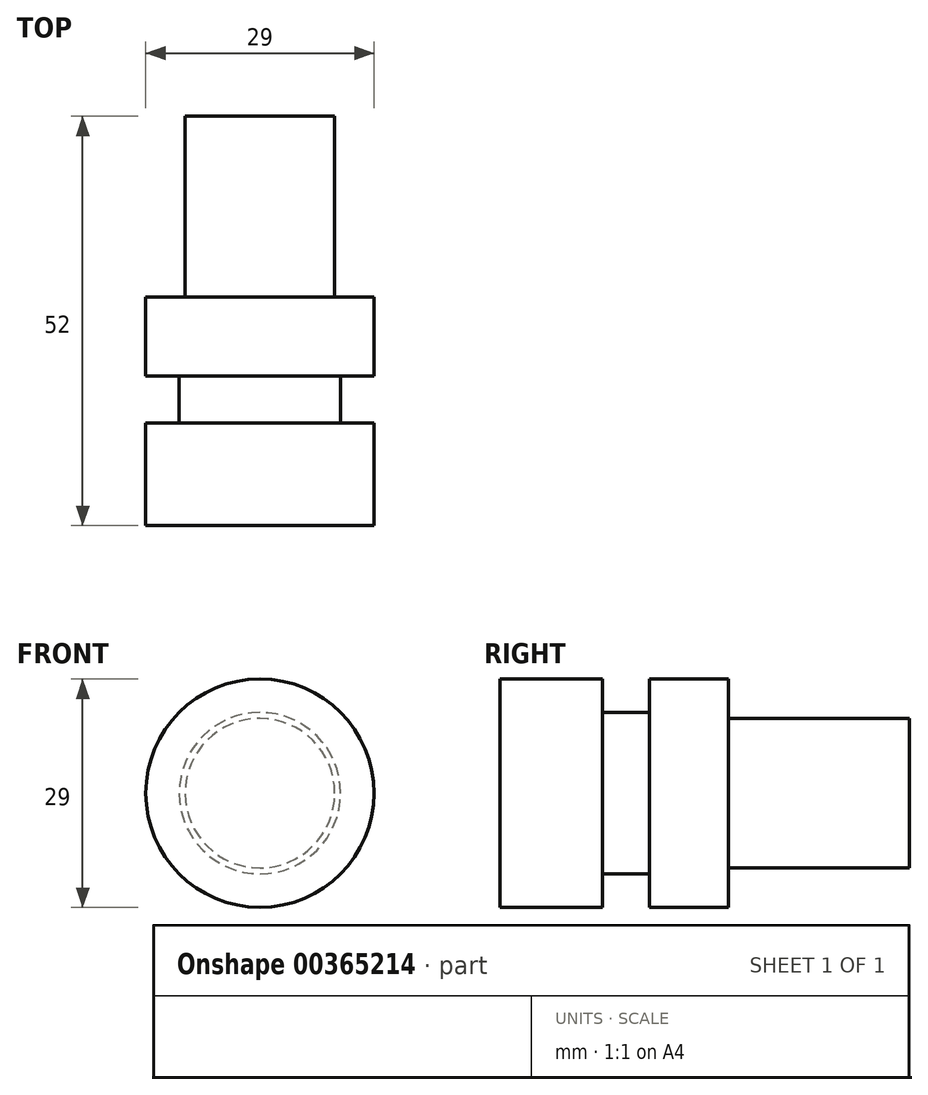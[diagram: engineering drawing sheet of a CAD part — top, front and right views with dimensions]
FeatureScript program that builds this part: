
annotation { "Feature Type Name" : "Feature", "Feature Type Description" : "" }
export const myFeature = defineFeature(function(context is Context, id is Id, definition is map)
    precondition{}
    {
        {
            var Q0;
            Q0=qCreatedBy(makeId("Front.planeOp"),FACE);
            var sketch = newSketch(context, id + "F0", { "sketchPlane" : qUnion([Q0])});
            skCircle(sketch, "E0", {"center": v(0, 0) * mm, "radius": 10.25 * mm});
            skSolve(sketch);
        }
        {
            var Q0;
            Q0 = qSketchRegion(id + "F0", true);
            extrude(context, id + "F1", {"entities" : qUnion([Q0]), "depth" : 6 * mm});
        }
        {
            var Q0;
            Q0=makeQuery(id+"F1.opExtrude","CAP_FACE",FACE,{"disambiguationData":[OSD([sQuery(id+"F0.wireOp",EDGE,"E0")])],"isStart":false});
            var sketch = newSketch(context, id + "F2", { "sketchPlane" : qUnion([Q0])});
            skCircle(sketch, "E1", {"center": v(0, 0) * mm, "radius": 14.5 * mm});
            skSolve(sketch);
        }
        {
            var Q0;
            Q0 = qSketchRegion(id + "F2", true);
            extrude(context, id + "F3", {"entities" : qUnion([Q0]), "operationType" : NewBodyOperationType.ADD, "depth" : 13 * mm});
        }
        {
            var Q0;
            Q0=makeQuery(id+"F1.opExtrude","CAP_FACE",FACE,{"disambiguationData":[OSD([sQuery(id+"F0.wireOp",EDGE,"E0")])],"isStart":true});
            var sketch = newSketch(context, id + "F4", { "sketchPlane" : qUnion([Q0])});
            skCircle(sketch, "E2", {"center": v(0, 0) * mm, "radius": 14.5 * mm});
            skSolve(sketch);
        }
        {
            var Q0;
            Q0 = qSketchRegion(id + "F4", true);
            extrude(context, id + "F5", {"entities" : qUnion([Q0]), "operationType" : NewBodyOperationType.ADD, "depth" : 10 * mm});
        }
        {
            var Q0;
            Q0=makeQuery(id+"F5.opExtrude","CAP_FACE",FACE,{"disambiguationData":[OSD([sQuery(id+"F4.wireOp",EDGE,"E2")])],"isStart":false});
            var sketch = newSketch(context, id + "F6", { "sketchPlane" : qUnion([Q0])});
            skCircle(sketch, "E3", {"center": v(0, 0) * mm, "radius": 9.5 * mm});
            skSolve(sketch);
        }
        {
            var Q0;
            Q0 = qSketchRegion(id + "F6", true);
            extrude(context, id + "F7", {"entities" : qUnion([Q0]), "operationType" : NewBodyOperationType.ADD, "depth" : 23 * mm});
        }
    });
